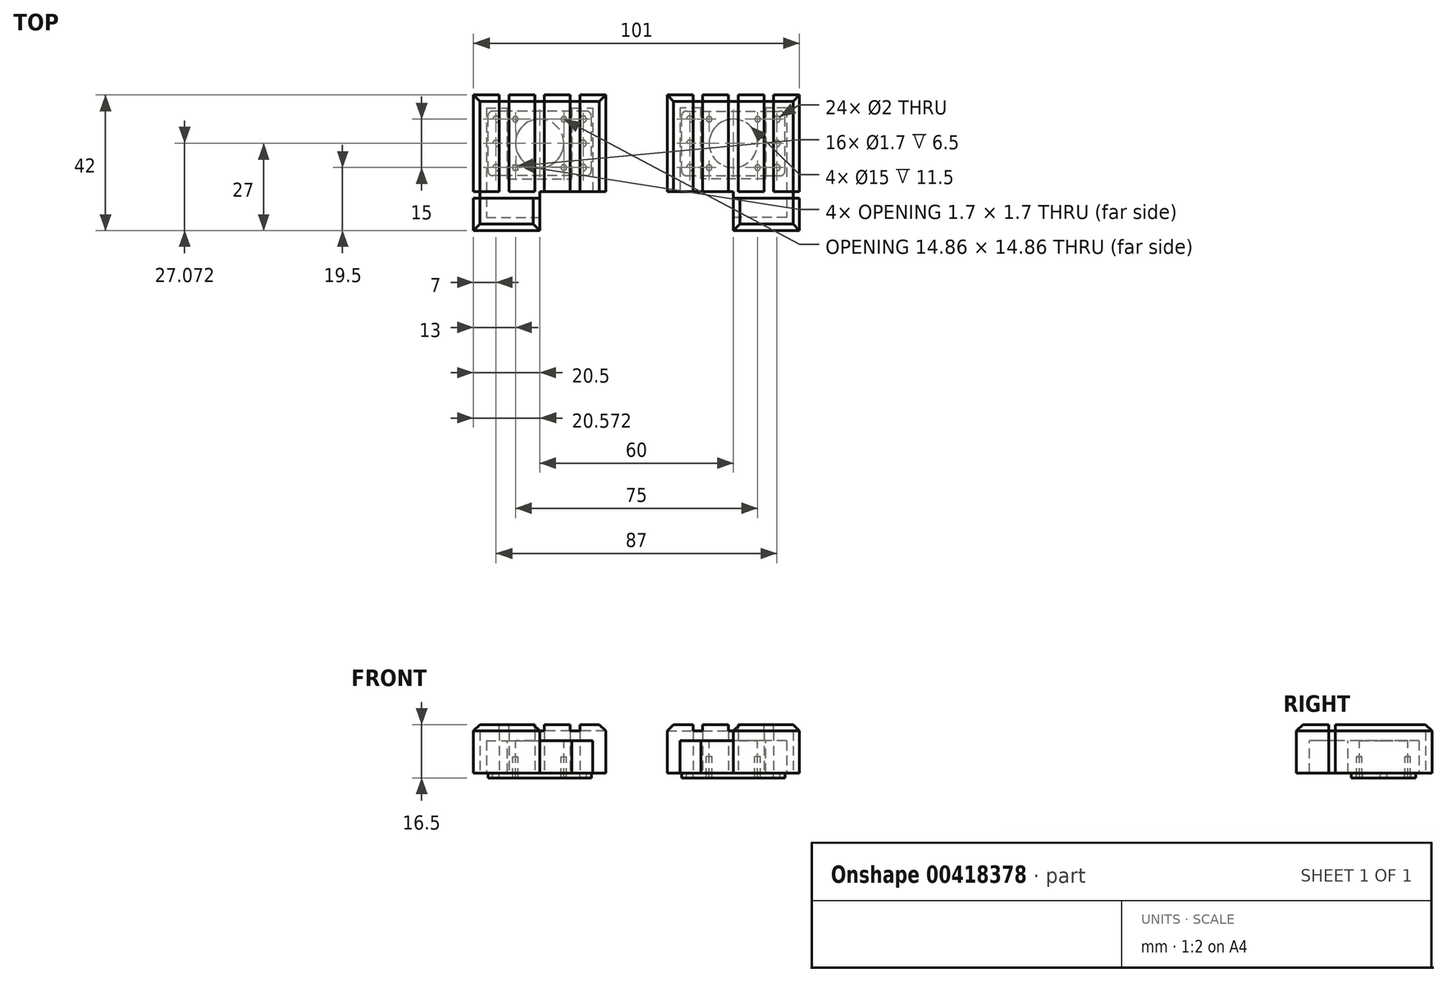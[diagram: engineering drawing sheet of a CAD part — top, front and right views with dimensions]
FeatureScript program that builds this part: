
annotation { "Feature Type Name" : "Feature", "Feature Type Description" : "" }
export const myFeature = defineFeature(function(context is Context, id is Id, definition is map)
    precondition{}
    {
        {
            var Q0;
            Q0=qCreatedBy(makeId("Top.planeOp"),FACE);
            var sketch = newSketch(context, id + "F0", { "sketchPlane" : qUnion([Q0])});
            skLineSegment(sketch, "E0.bottom", {"start": v(-20.5, 15) * mm, "end": v(20.5, 15) * mm});
            skLineSegment(sketch, "E0.top", {"start": v(-20.5, -15) * mm, "end": v(20.5, -15) * mm});
            skLineSegment(sketch, "E0.left", {"start": v(-20.5, 15) * mm, "end": v(-20.5, -15) * mm});
            skLineSegment(sketch, "E0.right", {"start": v(20.5, 15) * mm, "end": v(20.5, -15) * mm});
            skPoint(sketch, "E0.middle", {"position": v(0, 0) * mm});
            skLineSegment(sketch, "E1", {"start": v(-12.5, 15) * mm, "end": v(-12.5, -15) * mm});
            skLineSegment(sketch, "E2", {"start": v(-9.5, 15) * mm, "end": v(-9.5, -15) * mm});
            skLineSegment(sketch, "E3.MirrorCS", {"start": v(12.5, 15) * mm, "end": v(12.5, -15) * mm});
            skLineSegment(sketch, "E4.MirrorCS", {"start": v(9.5, 15) * mm, "end": v(9.5, -15) * mm});
            skLineSegment(sketch, "E5", {"start": v(-1.5, 15) * mm, "end": v(-1.5, -15) * mm});
            skLineSegment(sketch, "E6.MirrorCS", {"start": v(1.5, 15) * mm, "end": v(1.5, -15) * mm});
            skLineSegment(sketch, "E7", {"start": v(0, -15) * mm, "end": v(0, -27) * mm});
            skLineSegment(sketch, "E8", {"start": v(0, -27) * mm, "end": v(20.5, -27) * mm});
            skLineSegment(sketch, "E9", {"start": v(20.5, -27) * mm, "end": v(20.5, -15) * mm});
            skLineSegment(sketch, "E10", {"start": v(0, -17) * mm, "end": v(20.5, -17) * mm});
            skSolve(sketch);
        }
        {
            var Q0;
            Q0 = qSketchRegion(id + "F0", true);
            extrude(context, id + "F1", {"entities" : qUnion([Q0]), "oppositeDirection" : true, "depth" : 15 * mm, "offsetDistance" : 25 * mm});
        }
        {
            var Q0;
            {var subQ0=sQuery(id+"F0.wireOp",EDGE,"E1");Q0=makeQuery(id+"F0.imprint","IMPRINT",FACE,{"disambiguationData":[TD([[makeQuery(id+"F0.imprint","IMPRINT",EDGE,{"derivedFrom":subQ0}),1.0]])]});}
            var Q1;
            {var subQ0=sQuery(id+"F0.wireOp",EDGE,"E5");Q1=makeQuery(id+"F0.imprint","IMPRINT",FACE,{"disambiguationData":[TD([[makeQuery(id+"F0.imprint","IMPRINT",EDGE,{"derivedFrom":subQ0}),1.0]])]});}
            var Q2;
            {var subQ0=sQuery(id+"F0.wireOp",EDGE,"E3.MirrorCS");Q2=makeQuery(id+"F0.imprint","IMPRINT",FACE,{"disambiguationData":[TD([[makeQuery(id+"F0.imprint","IMPRINT",EDGE,{"derivedFrom":subQ0}),-1.0]])]});}
            var Q3;
            {var subQ8=sQuery(id+"F0.wireOp",EDGE,"E10");Q3=makeQuery(id+"F0.imprint","IMPRINT",FACE,{"disambiguationData":[TD([[makeQuery(id+"F0.imprint","IMPRINT",EDGE,{"derivedFrom":subQ8}),1.0]])]});}
            extrude(context, id + "F2", {"entities" : qUnion([Q0, Q1, Q2, Q3]), "operationType" : NewBodyOperationType.REMOVE, "oppositeDirection" : true, "depth" : 2 * mm, "offsetDistance" : 25 * mm});
        }
        {
            var Q0;
            {var subQ0=sQuery(id+"F0.wireOp",EDGE,"E0.bottom");var subQ1=sQuery(id+"F0.wireOp",EDGE,"E0.left");Q0=makeQuery(id+"F2.boolean.opBoolean","SPLIT",EDGE,{"disambiguationData":[TD([makeQuery(id+"F1.opExtrude","SWEPT_FACE",FACE,{"disambiguationData":[OSD([subQ1])]})])],"derivedFrom":makeQuery(id+"F1.opExtrude","CAP_EDGE",EDGE,{"disambiguationData":[OSD([subQ0])],"isStart":true})});}
            var Q1;
            Q1=makeQuery(id+"F1.opExtrude","CAP_EDGE",EDGE,{"disambiguationData":[OSD([sQuery(id+"F0.wireOp",EDGE,"E0.left")])],"isStart":true});
            var Q2;
            {var subQ0=sQuery(id+"F0.wireOp",EDGE,"E0.bottom");var subQ1=sQuery(id+"F0.wireOp",EDGE,"E9");var subQ2=sQuery(id+"F0.wireOp",EDGE,"E0.right");Q2=makeQuery(id+"F2.boolean.opBoolean","SPLIT",EDGE,{"disambiguationData":[TD([makeQuery(id+"F1.opExtrude","SWEPT_FACE",FACE,{"disambiguationData":[OSD([subQ0])]})])],"derivedFrom":makeQuery(id+"F1.opExtrude","CAP_EDGE",EDGE,{"disambiguationData":[OSD([subQ2,subQ1])],"isStart":true})});}
            var Q3;
            {var subQ0=sQuery(id+"F0.wireOp",EDGE,"E0.bottom");Q3=makeQuery(id+"F2.boolean.opBoolean","SPLIT",EDGE,{"disambiguationData":[TD([makeQuery(id+"F2.opExtrude","SWEPT_FACE",FACE,{"disambiguationData":[OSD([sQuery(id+"F0.wireOp",EDGE,"E3.MirrorCS")])]})])],"derivedFrom":makeQuery(id+"F1.opExtrude","CAP_EDGE",EDGE,{"disambiguationData":[OSD([subQ0])],"isStart":true})});}
            var Q4;
            {var subQ0=sQuery(id+"F0.wireOp",EDGE,"E0.bottom");Q4=makeQuery(id+"F2.boolean.opBoolean","SPLIT",EDGE,{"disambiguationData":[TD([makeQuery(id+"F2.opExtrude","SWEPT_FACE",FACE,{"disambiguationData":[OSD([sQuery(id+"F0.wireOp",EDGE,"E4.MirrorCS")])]})])],"derivedFrom":makeQuery(id+"F1.opExtrude","CAP_EDGE",EDGE,{"disambiguationData":[OSD([subQ0])],"isStart":true})});}
            var Q5;
            {var subQ0=sQuery(id+"F0.wireOp",EDGE,"E0.bottom");Q5=makeQuery(id+"F2.boolean.opBoolean","SPLIT",EDGE,{"disambiguationData":[TD([makeQuery(id+"F2.opExtrude","SWEPT_FACE",FACE,{"disambiguationData":[OSD([sQuery(id+"F0.wireOp",EDGE,"E2")])]})])],"derivedFrom":makeQuery(id+"F1.opExtrude","CAP_EDGE",EDGE,{"disambiguationData":[OSD([subQ0])],"isStart":true})});}
            var Q6;
            Q6=makeQuery(id+"F1.opExtrude","CAP_EDGE",EDGE,{"disambiguationData":[OSD([sQuery(id+"F0.wireOp",EDGE,"E8")])],"isStart":true});
            var Q7;
            {var subQ0=sQuery(id+"F0.wireOp",EDGE,"E9");var subQ1=sQuery(id+"F0.wireOp",EDGE,"E8");var subQ2=sQuery(id+"F0.wireOp",EDGE,"E0.right");Q7=makeQuery(id+"F2.boolean.opBoolean","SPLIT",EDGE,{"disambiguationData":[TD([makeQuery(id+"F1.opExtrude","SWEPT_FACE",FACE,{"disambiguationData":[OSD([subQ1])]})])],"derivedFrom":makeQuery(id+"F1.opExtrude","CAP_EDGE",EDGE,{"disambiguationData":[OSD([subQ2,subQ0])],"isStart":true})});}
            var Q8;
            Q8=makeQuery(id+"F1.opExtrude","CAP_EDGE",EDGE,{"disambiguationData":[OSD([sQuery(id+"F0.wireOp",EDGE,"E7")])],"isStart":true});
            chamfer(context, id + "F3", {"entities" : qUnion([Q0, Q1, Q2, Q3, Q4, Q5, Q6, Q7, Q8]), "width" : 2 * mm, "tangentPropagation" : true});
        }
        {
            var Q0;
            {var subQ0=sQuery(id+"F0.wireOp",EDGE,"E0.bottom");var subQ1=sQuery(id+"F0.wireOp",EDGE,"E4.MirrorCS");var subQ2=sQuery(id+"F0.wireOp",EDGE,"E0.top");Q0=makeQuery(id+"F2.boolean.opBoolean","SPLIT",FACE,{"disambiguationData":[TD([makeQuery(id+"F2.opExtrude","SWEPT_FACE",FACE,{"disambiguationData":[OSD([subQ1])]})])],"derivedFrom":makeQuery(id+"F1.opExtrude","CAP_FACE",FACE,{"disambiguationData":[OSD([subQ0,subQ2,sQuery(id+"F0.wireOp",EDGE,"E0.left"),sQuery(id+"F0.wireOp",EDGE,"E0.right"),sQuery(id+"F0.wireOp",EDGE,"E7"),sQuery(id+"F0.wireOp",EDGE,"E8"),sQuery(id+"F0.wireOp",EDGE,"E9")])],"isStart":true})});}
            var sketch = newSketch(context, id + "F4", { "sketchPlane" : qUnion([Q0])});
            skCircle(sketch, "E11", {"center": v(-7.5, 7.5) * mm, "radius": 0.85 * mm});
            skCircle(sketch, "E12.MirrorC", {"center": v(7.5, 7.5) * mm, "radius": 0.85 * mm});
            skCircle(sketch, "E13.MirrorC", {"center": v(7.5, -7.5) * mm, "radius": 0.85 * mm});
            skCircle(sketch, "E14.MirrorC", {"center": v(-7.5, -7.5) * mm, "radius": 0.85 * mm});
            skSolve(sketch);
        }
        {
            var Q0;
            Q0 = qSketchRegion(id + "F4", true);
            extrude(context, id + "F5", {"entities" : qUnion([Q0]), "operationType" : NewBodyOperationType.REMOVE, "endBound" : BoundingType.THROUGH_ALL, "oppositeDirection" : true, "depth" : 25 * mm, "offsetDistance" : 25 * mm});
        }
        {
            var Q0;
            Q0=makeQuery(id+"F1.opExtrude","CAP_FACE",FACE,{"disambiguationData":[OSD([sQuery(id+"F0.wireOp",EDGE,"E0.bottom"),sQuery(id+"F0.wireOp",EDGE,"E0.top"),sQuery(id+"F0.wireOp",EDGE,"E0.left"),sQuery(id+"F0.wireOp",EDGE,"E0.right"),sQuery(id+"F0.wireOp",EDGE,"E7"),sQuery(id+"F0.wireOp",EDGE,"E8"),sQuery(id+"F0.wireOp",EDGE,"E9")])],"isStart":false});
            var sketch = newSketch(context, id + "F6", { "sketchPlane" : qUnion([Q0])});
            skLineSegment(sketch, "E15.bottom", {"start": v(8.5, 16) * mm, "end": v(-8.5, 16) * mm});
            skLineSegment(sketch, "E15.top", {"start": v(8.5, -16) * mm, "end": v(-8.5, -16) * mm});
            skLineSegment(sketch, "E15.left", {"start": v(10, 14.5) * mm, "end": v(10, -14.5) * mm});
            skLineSegment(sketch, "E15.right", {"start": v(-10, 14.5) * mm, "end": v(-10, -14.5) * mm});
            skPoint(sketch, "E15.middle", {"position": v(0, 0) * mm});
            skCircle(sketch, "E16", {"center": v(0, 13.5) * mm, "radius": 1 * mm});
            skCircle(sketch, "E17", {"center": v(7.5, 13.5) * mm, "radius": 1 * mm});
            skCircle(sketch, "E18.MirrorC", {"center": v(-7.5, 13.5) * mm, "radius": 1 * mm});
            skCircle(sketch, "E19.MirrorC", {"center": v(7.5, -13.5) * mm, "radius": 1 * mm});
            skCircle(sketch, "E20.MirrorC", {"center": v(-7.5, -13.5) * mm, "radius": 1 * mm});
            skCircle(sketch, "E21.MirrorC", {"center": v(0, -13.5) * mm, "radius": 1 * mm});
            skPoint(sketch, "E22.visualSharp", {"position": v(10, 16) * mm});
            skArc(sketch, "E22.filletArc", {"start": v(10, 14.5) * mm, "mid": v(9.56, 15.56) * mm, "end": v(8.5, 16) * mm});
            skPoint(sketch, "E23.visualSharp", {"position": v(10, -16) * mm});
            skArc(sketch, "E23.filletArc", {"start": v(8.5, -16) * mm, "mid": v(9.56, -15.56) * mm, "end": v(10, -14.5) * mm});
            skPoint(sketch, "E24.visualSharp", {"position": v(-10, -16) * mm});
            skArc(sketch, "E24.filletArc", {"start": v(-10, -14.5) * mm, "mid": v(-9.56, -15.56) * mm, "end": v(-8.5, -16) * mm});
            skPoint(sketch, "E25.visualSharp", {"position": v(-10, 16) * mm});
            skArc(sketch, "E25.filletArc", {"start": v(-8.5, 16) * mm, "mid": v(-9.56, 15.56) * mm, "end": v(-10, 14.5) * mm});
            skCircle(sketch, "E26", {"center": v(0, 0) * mm, "radius": 7.5 * mm});
            skSolve(sketch);
        }
        {
            var Q0;
            Q0 = qSketchRegion(id + "F6", true);
            extrude(context, id + "F7", {"entities" : qUnion([Q0]), "depth" : 1.5 * mm, "offsetDistance" : 25 * mm});
        }
        {
            var Q0;
            Q0=makeQuery(id+"F1.opExtrude","SWEPT_FACE",FACE,{"disambiguationData":[OSD([sQuery(id+"F0.wireOp",EDGE,"E0.bottom")])]});
            var sketch = newSketch(context, id + "F8", { "sketchPlane" : qUnion([Q0])});
            skLineSegment(sketch, "E27", {"start": v(12.5, -2) * mm, "end": v(12.5, -15) * mm});
            skLineSegment(sketch, "E28", {"start": v(9.5, -2) * mm, "end": v(9.5, -15) * mm});
            skLineSegment(sketch, "E29", {"start": v(9.5, -15) * mm, "end": v(12.5, -15) * mm});
            skLineSegment(sketch, "E30", {"start": v(12.5, -2) * mm, "end": v(9.5, -2) * mm});
            skLineSegment(sketch, "E31", {"start": v(1.5, -2) * mm, "end": v(1.5, -15) * mm});
            skLineSegment(sketch, "E32", {"start": v(1.5, -15) * mm, "end": v(0, -15) * mm});
            skLineSegment(sketch, "E33", {"start": v(1.5, -2) * mm, "end": v(0, -2) * mm});
            skLineSegment(sketch, "E34.MirrorCS", {"start": v(-1.5, -2) * mm, "end": v(0, -2) * mm});
            skLineSegment(sketch, "E35.MirrorCS", {"start": v(-1.5, -15) * mm, "end": v(0, -15) * mm});
            skLineSegment(sketch, "E36.MirrorCS", {"start": v(-9.5, -15) * mm, "end": v(-12.5, -15) * mm});
            skLineSegment(sketch, "E37.MirrorCS", {"start": v(-12.5, -2) * mm, "end": v(-12.5, -15) * mm});
            skLineSegment(sketch, "E38.MirrorCS", {"start": v(-1.5, -2) * mm, "end": v(-1.5, -15) * mm});
            skLineSegment(sketch, "E39.MirrorCS", {"start": v(-12.5, -2) * mm, "end": v(-9.5, -2) * mm});
            skLineSegment(sketch, "E40.MirrorCS", {"start": v(-9.5, -2) * mm, "end": v(-9.5, -15) * mm});
            skSolve(sketch);
        }
        {
            var Q0;
            Q0 = qSketchRegion(id + "F8", true);
            extrude(context, id + "F9", {"entities" : qUnion([Q0]), "operationType" : NewBodyOperationType.REMOVE, "oppositeDirection" : true, "depth" : 2 * mm, "offsetDistance" : 25 * mm});
        }
        {
            var Q0;
            Q0=makeQuery(id+"F1.opExtrude","SWEPT_FACE",FACE,{"disambiguationData":[OSD([sQuery(id+"F0.wireOp",EDGE,"E0.right"),sQuery(id+"F0.wireOp",EDGE,"E9")])]});
            var sketch = newSketch(context, id + "F10", { "sketchPlane" : qUnion([Q0])});
            skLineSegment(sketch, "E41.bottom", {"start": v(-15, -2) * mm, "end": v(-17, -2) * mm});
            skLineSegment(sketch, "E41.top", {"start": v(-15, -15) * mm, "end": v(-17, -15) * mm});
            skLineSegment(sketch, "E41.left", {"start": v(-15, -2) * mm, "end": v(-15, -15) * mm});
            skLineSegment(sketch, "E41.right", {"start": v(-17, -2) * mm, "end": v(-17, -15) * mm});
            skSolve(sketch);
        }
        {
            var Q0;
            Q0 = qSketchRegion(id + "F10", true);
            extrude(context, id + "F11", {"entities" : qUnion([Q0]), "operationType" : NewBodyOperationType.REMOVE, "oppositeDirection" : true, "depth" : 2 * mm, "offsetDistance" : 25 * mm});
        }
        {
            var Q0;
            Q0=makeQuery(id+"F7.opExtrude","SWEPT_BODY",BODY,{"disambiguationData":[OSD([sQuery(id+"F6.wireOp",EDGE,"E15.bottom"),sQuery(id+"F6.wireOp",EDGE,"E15.top"),sQuery(id+"F6.wireOp",EDGE,"E15.left"),sQuery(id+"F6.wireOp",EDGE,"E15.right"),sQuery(id+"F6.wireOp",EDGE,"E16"),sQuery(id+"F6.wireOp",EDGE,"E18.MirrorC"),sQuery(id+"F6.wireOp",EDGE,"E17"),sQuery(id+"F6.wireOp",EDGE,"E19.MirrorC"),sQuery(id+"F6.wireOp",EDGE,"E20.MirrorC"),sQuery(id+"F6.wireOp",EDGE,"E21.MirrorC"),sQuery(id+"F6.wireOp",EDGE,"E22.filletArc"),sQuery(id+"F6.wireOp",EDGE,"E23.filletArc"),sQuery(id+"F6.wireOp",EDGE,"E24.filletArc"),sQuery(id+"F6.wireOp",EDGE,"E25.filletArc"),sQuery(id+"F6.wireOp",EDGE,"E26")])]});
            var Q1;
            Q1=makeQuery(id+"F7.opExtrude","CAP_EDGE",EDGE,{"disambiguationData":[OSD([sQuery(id+"F6.wireOp",EDGE,"E26")])],"isStart":true});
            transform(context, id + "F12", {"entities" : qUnion([Q0]), "transformType" : TransformType.ROTATION, "transformAxis" : qUnion([Q1]), "angle" : 90 * degree, "makeCopy" : false});
        }
        {
            var Q0;
            Q0=makeQuery(id+"F7.opExtrude","CAP_FACE",FACE,{"disambiguationData":[OSD([sQuery(id+"F6.wireOp",EDGE,"E15.bottom"),sQuery(id+"F6.wireOp",EDGE,"E15.top"),sQuery(id+"F6.wireOp",EDGE,"E15.left"),sQuery(id+"F6.wireOp",EDGE,"E15.right"),sQuery(id+"F6.wireOp",EDGE,"E16"),sQuery(id+"F6.wireOp",EDGE,"E18.MirrorC"),sQuery(id+"F6.wireOp",EDGE,"E17"),sQuery(id+"F6.wireOp",EDGE,"E19.MirrorC"),sQuery(id+"F6.wireOp",EDGE,"E20.MirrorC"),sQuery(id+"F6.wireOp",EDGE,"E21.MirrorC"),sQuery(id+"F6.wireOp",EDGE,"E22.filletArc"),sQuery(id+"F6.wireOp",EDGE,"E23.filletArc"),sQuery(id+"F6.wireOp",EDGE,"E24.filletArc"),sQuery(id+"F6.wireOp",EDGE,"E25.filletArc"),sQuery(id+"F6.wireOp",EDGE,"E26")])],"isStart":false});
            var sketch = newSketch(context, id + "F13", { "sketchPlane" : qUnion([Q0])});
            skCircle(sketch, "E42.0", {"center": v(-7.5, -7.5) * mm, "radius": 0.85 * mm});
            skCircle(sketch, "E43.0", {"center": v(7.5, -7.5) * mm, "radius": 0.85 * mm});
            skCircle(sketch, "E44.0", {"center": v(-7.5, 7.5) * mm, "radius": 0.85 * mm});
            skCircle(sketch, "E45.0", {"center": v(7.5, 7.5) * mm, "radius": 0.85 * mm});
            skSolve(sketch);
        }
        {
            var Q0;
            Q0 = qSketchRegion(id + "F13", true);
            extrude(context, id + "F14", {"entities" : qUnion([Q0]), "operationType" : NewBodyOperationType.REMOVE, "endBound" : BoundingType.UP_TO_NEXT, "oppositeDirection" : true, "depth" : 25 * mm, "offsetDistance" : 25 * mm});
        }
        {
            var Q0;
            Q0=makeQuery(id+"F1.opExtrude","CAP_FACE",FACE,{"disambiguationData":[OSD([sQuery(id+"F0.wireOp",EDGE,"E0.bottom"),sQuery(id+"F0.wireOp",EDGE,"E0.top"),sQuery(id+"F0.wireOp",EDGE,"E0.left"),sQuery(id+"F0.wireOp",EDGE,"E0.right"),sQuery(id+"F0.wireOp",EDGE,"E7"),sQuery(id+"F0.wireOp",EDGE,"E8"),sQuery(id+"F0.wireOp",EDGE,"E9")])],"isStart":false});
            var sketch = newSketch(context, id + "F15", { "sketchPlane" : qUnion([Q0])});
            skLineSegment(sketch, "E46.bottom", {"start": v(16.5, -11) * mm, "end": v(-16.5, -11) * mm});
            skLineSegment(sketch, "E46.top", {"start": v(16.5, 23) * mm, "end": v(-16.5, 23) * mm});
            skLineSegment(sketch, "E46.left", {"start": v(16.5, -11) * mm, "end": v(16.5, 23) * mm});
            skLineSegment(sketch, "E46.right", {"start": v(-16.5, -11) * mm, "end": v(-16.5, 23) * mm});
            skSolve(sketch);
        }
        {
            var Q0;
            Q0 = qSketchRegion(id + "F15", true);
            extrude(context, id + "F16", {"entities" : qUnion([Q0]), "operationType" : NewBodyOperationType.REMOVE, "oppositeDirection" : true, "depth" : 10 * mm, "offsetDistance" : 25 * mm});
        }
        {
            var Q0;
            Q0=makeQuery(id+"F16.boolean.opBoolean","COPY",FACE,{"derivedFrom":makeQuery(id+"F16.opExtrude","CAP_FACE",FACE,{"disambiguationData":[OSD([sQuery(id+"F15.wireOp",EDGE,"E46.bottom"),sQuery(id+"F15.wireOp",EDGE,"E46.top"),sQuery(id+"F15.wireOp",EDGE,"E46.left"),sQuery(id+"F15.wireOp",EDGE,"E46.right")])],"isStart":false})});
            var sketch = newSketch(context, id + "F17", { "sketchPlane" : qUnion([Q0])});
            skLineSegment(sketch, "E47.bottom", {"start": v(10, -11) * mm, "end": v(-10, -11) * mm});
            skLineSegment(sketch, "E47.top", {"start": v(10, 11) * mm, "end": v(-10, 11) * mm});
            skLineSegment(sketch, "E47.left", {"start": v(10, -11) * mm, "end": v(10, 11) * mm});
            skLineSegment(sketch, "E47.right", {"start": v(-10, -11) * mm, "end": v(-10, 11) * mm});
            skPoint(sketch, "E47.middle", {"position": v(0, 0) * mm});
            skPoint(sketch, "E48", {"position": v(7.5, 7.5) * mm});
            skCircle(sketch, "E49.0", {"center": v(7.5, -7.5) * mm, "radius": 0.85 * mm});
            skCircle(sketch, "E50.0", {"center": v(-7.5, -7.5) * mm, "radius": 0.85 * mm});
            skCircle(sketch, "E51.0", {"center": v(-7.5, 7.5) * mm, "radius": 0.85 * mm});
            skCircle(sketch, "E52.0", {"center": v(7.5, 7.5) * mm, "radius": 0.85 * mm});
            skCircle(sketch, "E53", {"center": v(0, 0) * mm, "radius": 7.5 * mm});
            skSolve(sketch);
        }
        {
            var Q0;
            Q0 = qSketchRegion(id + "F17", true);
            var Q1;
            Q1=makeQuery(id+"F1.opExtrude","CAP_FACE",FACE,{"disambiguationData":[OSD([sQuery(id+"F0.wireOp",EDGE,"E0.bottom"),sQuery(id+"F0.wireOp",EDGE,"E0.top"),sQuery(id+"F0.wireOp",EDGE,"E0.left"),sQuery(id+"F0.wireOp",EDGE,"E0.right"),sQuery(id+"F0.wireOp",EDGE,"E7"),sQuery(id+"F0.wireOp",EDGE,"E8"),sQuery(id+"F0.wireOp",EDGE,"E9")])],"isStart":false});
            extrude(context, id + "F18", {"entities" : qUnion([Q0]), "operationType" : NewBodyOperationType.ADD, "endBound" : BoundingType.UP_TO_SURFACE, "depth" : 25 * mm, "endBoundEntityFace" : qUnion([Q1]), "offsetDistance" : 25 * mm});
        }
        {
            var Q0;
            {var subQ0=sQuery(id+"F0.wireOp",EDGE,"E0.bottom");var subQ1=sQuery(id+"F0.wireOp",EDGE,"E0.top");Q0=makeQuery(id+"F2.boolean.opBoolean","SPLIT",FACE,{"disambiguationData":[TD([makeQuery(id+"F2.opExtrude","SWEPT_FACE",FACE,{"disambiguationData":[OSD([sQuery(id+"F0.wireOp",EDGE,"E2")])]})])],"derivedFrom":makeQuery(id+"F1.opExtrude","CAP_FACE",FACE,{"disambiguationData":[OSD([subQ0,subQ1,sQuery(id+"F0.wireOp",EDGE,"E0.left"),sQuery(id+"F0.wireOp",EDGE,"E0.right"),sQuery(id+"F0.wireOp",EDGE,"E7"),sQuery(id+"F0.wireOp",EDGE,"E8"),sQuery(id+"F0.wireOp",EDGE,"E9")])],"isStart":true})});}
            var sketch = newSketch(context, id + "F19", { "sketchPlane" : qUnion([Q0])});
            skCircle(sketch, "E54.0", {"center": v(7.5, 7.5) * mm, "radius": 0.85 * mm});
            skCircle(sketch, "E55.0", {"center": v(-7.5, 7.5) * mm, "radius": 0.85 * mm});
            skCircle(sketch, "E56.0", {"center": v(-7.5, -7.5) * mm, "radius": 0.85 * mm});
            skCircle(sketch, "E57.0", {"center": v(7.5, -7.5) * mm, "radius": 0.85 * mm});
            skSolve(sketch);
        }
        {
            var Q0;
            Q0 = qSketchRegion(id + "F19", true);
            extrude(context, id + "F20", {"entities" : qUnion([Q0]), "operationType" : NewBodyOperationType.ADD, "oppositeDirection" : true, "depth" : 10 * mm, "offsetDistance" : 25 * mm});
        }
        {
            var Q0;
            Q0=qCreatedBy(makeId("Right.planeOp"),FACE);
            cPlane(context, id + "F21", {"entities" : qUnion([Q0]), "cplaneType" : CPlaneType.OFFSET, "offset" : 30 * mm, "oppositeDirection" : true, "width" : 150 * mm, "height" : 150 * mm});
        }
        {
            var Q0;
            Q0=makeQuery(id+"F1.opExtrude","SWEPT_BODY",BODY,{"disambiguationData":[OSD([sQuery(id+"F0.wireOp",EDGE,"E0.bottom"),sQuery(id+"F0.wireOp",EDGE,"E0.top"),sQuery(id+"F0.wireOp",EDGE,"E0.left"),sQuery(id+"F0.wireOp",EDGE,"E0.right"),sQuery(id+"F0.wireOp",EDGE,"E7"),sQuery(id+"F0.wireOp",EDGE,"E8"),sQuery(id+"F0.wireOp",EDGE,"E9")])]});
            var Q1;
            Q1=qCreatedBy(id+"F21.planeOp",FACE);
            mirror(context, id + "F22", {"entities" : qUnion([Q0]), "mirrorPlane" : qUnion([Q1])});
        }
    });
